# Revit family: Faucet-Wall_Mount-Bath_Spout-KOHLER-Bancroft-K-10588
name_source: partatom
category: Plumbing Fixtures
revit_build: Autodesk Revit 2015 (Build: 20140606_1530(x64)
units: mm (PartAtom-declared; Revit-internal decimal feet)

## types (5) — shared parameters
ADA Compliant = No
Assembly Code = D2010
CW Connection = No
Cold Water Inlet = Cold Water Inlet
Date Modified = 11/19/2018
Default Elevation = 36"
Description = Wall-mount diverter bath spout
Drain Included = No
Flow Rate = 0 GPM
HW Connection = Yes
Height = 2 3/4"
Hot Water Inlet = Hot Water Inlet
Length = 5 3/4"
Manufacturer = KOHLER Co.
MasterFormat 1995 = 15410
MasterFormat 2004 = 22.41.39
Material = Premium Metal Construction
Pressure = 0.00 psi
Product Documentation Link = http://www.us.kohler.com
Product Name = Bancroft
Product Page URL = http://www.us.kohler.com
Spout Reach = 5 3/4"
Tempered Water = Tempered Water Inlet
URL = https://www.us.kohler.com
Vent Connection = No
Waste Connection = No
Waste Water Outlet = Waste Water Outlet
Width = 2 3/4"

## per-type parameters (varying)
| type | Finish | Model | Type |
| CP-Polished Chrome | Kohler-Metal-CP-Polished_Chrome | K-10588-CP | 1 |
| SN-Vibrant Polished Chrome | Kohler-Metal-SN-Vibrant_Polished_Nickel | K-10588-SN | 2 |
| BN-Vibrant Brushed Nickel | Kohler-Metal-BN-Vibrant_Brushed_Nickel | K-10588-BN | 3 |
| BV-Vibrant Brushed Bronze | Kohler-Metal-BV-Brushed_Bronze | K-10588-BV | 4 |
| 2BZ-Oil-Rubbed Bronze | Kohler-Metal-2BZ-Oil_Rubbed_Bronze | K-10588-2BZ | 5 |

## geometry (parser evidence)
native form markers: Sweep x6
no freeform markers — native parametric forms only
